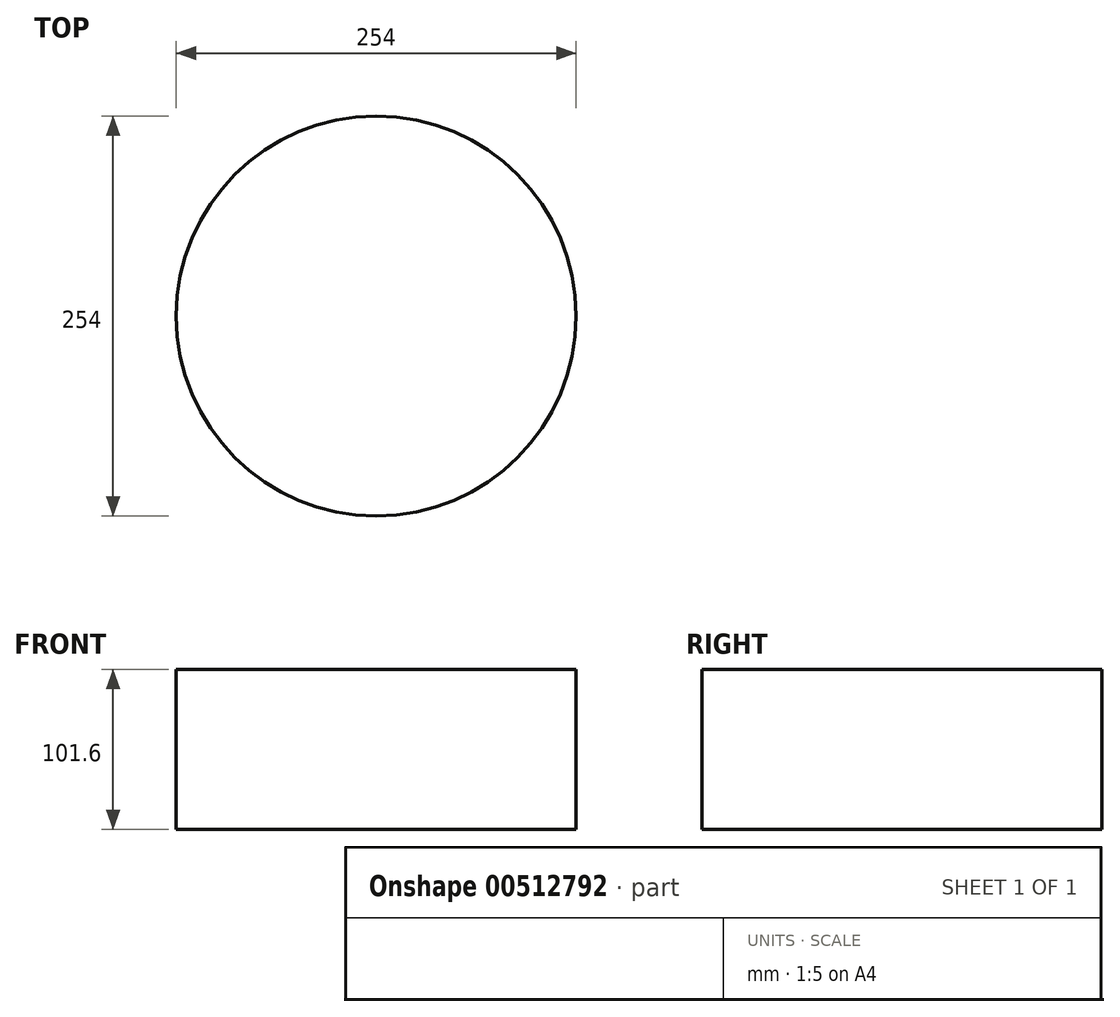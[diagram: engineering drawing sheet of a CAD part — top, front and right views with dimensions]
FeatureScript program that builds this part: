
annotation { "Feature Type Name" : "Feature", "Feature Type Description" : "" }
export const myFeature = defineFeature(function(context is Context, id is Id, definition is map)
    precondition{}
    {
        {
            var Q0;
            Q0=qCreatedBy(makeId("Top.planeOp"),FACE);
            var sketch = newSketch(context, id + "F0", { "sketchPlane" : qUnion([Q0])});
            skCircle(sketch, "E0", {"center": v(0, 0) * mm, "radius": 127 * mm});
            skSolve(sketch);
        }
        {
            var Q0;
            Q0=qSketchRegion(id+"F0",true);
            extrude(context, id + "F1", {"entities" : qUnion([Q0]), "depth" : 101.6 * mm});
        }
    });
